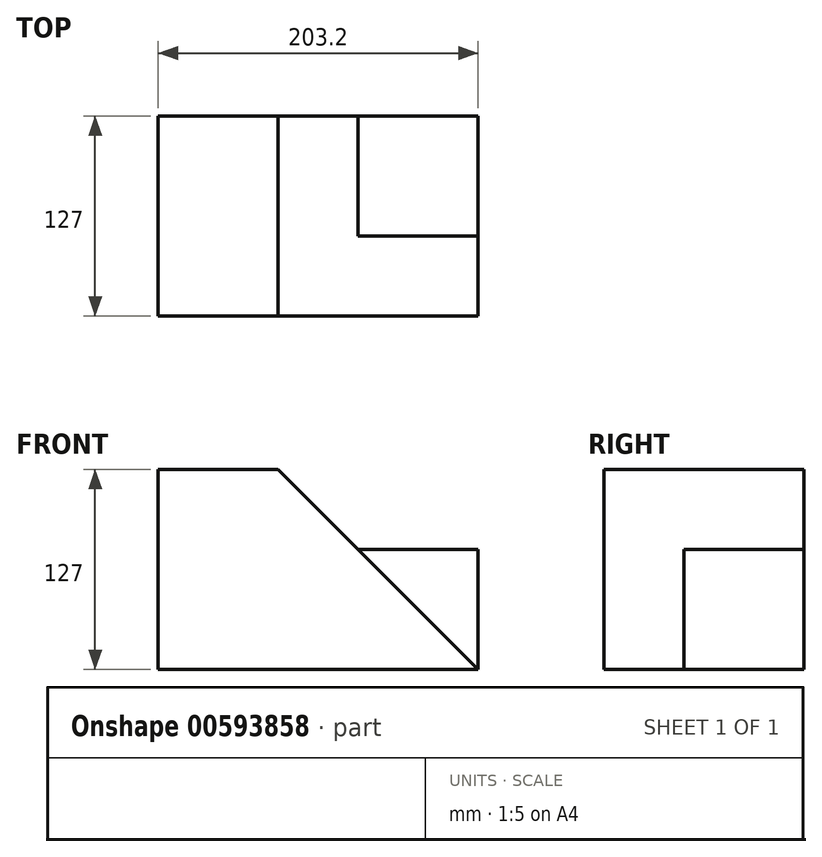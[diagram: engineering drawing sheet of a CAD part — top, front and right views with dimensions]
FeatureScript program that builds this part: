
annotation { "Feature Type Name" : "Feature", "Feature Type Description" : "" }
export const myFeature = defineFeature(function(context is Context, id is Id, definition is map)
    precondition{}
    {
        {
            var Q0;
            Q0=qCreatedBy(makeId("Front.planeOp"),FACE);
            var sketch = newSketch(context, id + "F0", { "sketchPlane" : qUnion([Q0])});
            skLineSegment(sketch, "E0", {"start": v(0, 0) * mm, "end": v(0, 127) * mm});
            skLineSegment(sketch, "E1", {"start": v(0, 127) * mm, "end": v(76.2, 127) * mm});
            skLineSegment(sketch, "E2", {"start": v(76.2, 127) * mm, "end": v(203.2, 0) * mm});
            skLineSegment(sketch, "E3", {"start": v(203.2, 0) * mm, "end": v(0, 0) * mm});
            skLineSegment(sketch, "E4", {"start": v(203.2, 0) * mm, "end": v(203.2, 76.2) * mm});
            skLineSegment(sketch, "E5", {"start": v(203.2, 76.2) * mm, "end": v(127, 76.2) * mm});
            skSolve(sketch);
        }
        {
            var Q0;
            Q0=makeQuery(id+"F0.imprint","IMPRINT",FACE,{"disambiguationData":[TD([[makeQuery(id+"F0.imprint","IMPRINT",EDGE,{"derivedFrom":sQuery(id+"F0.wireOp",EDGE,"E0")}),-1.0]])]});
            extrude(context, id + "F1", {"entities" : qUnion([Q0]), "depth" : 127 * mm, "offsetDistance" : 25.4 * mm});
        }
        {
            var Q0;
            {var subQ0=sQuery(id+"F0.wireOp",EDGE,"E4");Q0=makeQuery(id+"F0.imprint","IMPRINT",FACE,{"disambiguationData":[TD([[makeQuery(id+"F0.imprint","IMPRINT",EDGE,{"derivedFrom":subQ0}),1.0]])]});}
            extrude(context, id + "F2", {"entities" : qUnion([Q0]), "operationType" : NewBodyOperationType.ADD, "depth" : 76.2 * mm, "offsetDistance" : 25.4 * mm});
        }
    });
